# Revit family: MINI_GAMMA-IP30-syst-AT-de
name_source: partatom
category: Electrical Equipment
units: mm (PartAtom-declared; Revit-internal decimal feet)

## family parameters
Cut with Voids When Loaded = No
Host = Face
Panel Configuration = Two Columns, Circuits Across
Part Type = Panelboard
Room Calculation Point = No
Round Connector Dimension = Use Diameter
Shared = No

## types (5) — shared parameters
EF000003 - Montageart = EV000384 - Aufputz
EF000007 - Farbe = EV000202 - weiß
EF000049 - Tiefe = 82 mm  [stored 0.269029 ft]
EF000116 - RAL-Nummer = 9010
EF000118 - Mit Montageplatte = No
EF000266 - Anzahl der Reihen = 1
EF000339 - Art der Abdeckung = EV005746 - optional
EF001062 - EMV-Ausführung = No
EF001131 - Innentiefe = 82 mm  [stored 0.269029 ft]
EF001134 - DIN-Schiene = No
EF001596 - Werkstoff des Gehäuses = EV000139 - Kunststoff
EF004462 - Art der Schließung = EV000154 - sonstige
EF005474 - Schutzart (IP) = EV006410 - IP30
EF006244 - Transparenter Deckel/Tür = No
EF006306 - Mit Schloss = No
EF009212 - Ausführung Deckel = EV009916 - mit Ausschnitt
EF015776 - Erdungsklemmenblock = No
EF015777 - Neutralleiterklemmenblock = No
EF015941 - Signaldurchlassende Tür = No
HG000001 - Anzahl der Spalten = 1
HG000002 - Mit tür = No
HG000003 - Bereich = mini gamma
HG000005 - Dicke = 3 mm  [stored 0.00984252 ft]
HG000006 - Unterputz = No
HG000009 - Doppelflügeligen Tür = No
HG000010 - Asymmetrische Türen = No
HG000011 - Leere Reihen von unten = No
Manufacturer = Hager
Type Comments = mini gamma
zero-valued in all types: Default Elevation, EF000218 - Einbautiefe, EF000332 - Einbauhöhe, EF000846 - Einbaubreite, HG000007 - Anzahl der leeren Spalten, HG000008 - Anzahl der leeren Reihen

## per-type parameters (varying)
| type | EF000008 - Breite | EF000040 - Höhe | EF001088 - Anbaumöglichkeit | EF002950 - Breite in Teilungseinheiten | HG000004 - Herstellerreferenz | Model |
| Aufputz IP30 B110 H180 T82 4 Teilungseinheiten - GD104N | 110 mm | 180 mm | No | 4 | GD104N | GD104N |
| Aufputz IP30 B146 H180 T82 6 Teilungseinheiten - GD106N | 146 mm | 180 mm | Yes | 6 | GD106N | GD106N |
| Aufputz IP30 B182 H180 T82 8 Teilungseinheiten - GD108N | 182 mm | 180 mm | Yes | 8 | GD108N | GD108N |
| Aufputz IP30 B218 H180 T82 10 Teilungseinheiten - GD110N | 218 mm | 180 mm | Yes | 10 | GD110N | GD110N |
| Aufputz IP30 B55 H160 T82 2 Teilungseinheiten - GD102N | 55 mm  [stored 0.180446 ft] | 160 mm  [stored 0.524934 ft] | No | 2 | GD102N | GD102N |

note: [stored X ft] marks values corroborated as IEEE doubles in the binary element streams (Revit-internal decimal feet)

## geometry (parser evidence)
native form markers: Sweep x12
no freeform markers — native parametric forms only
